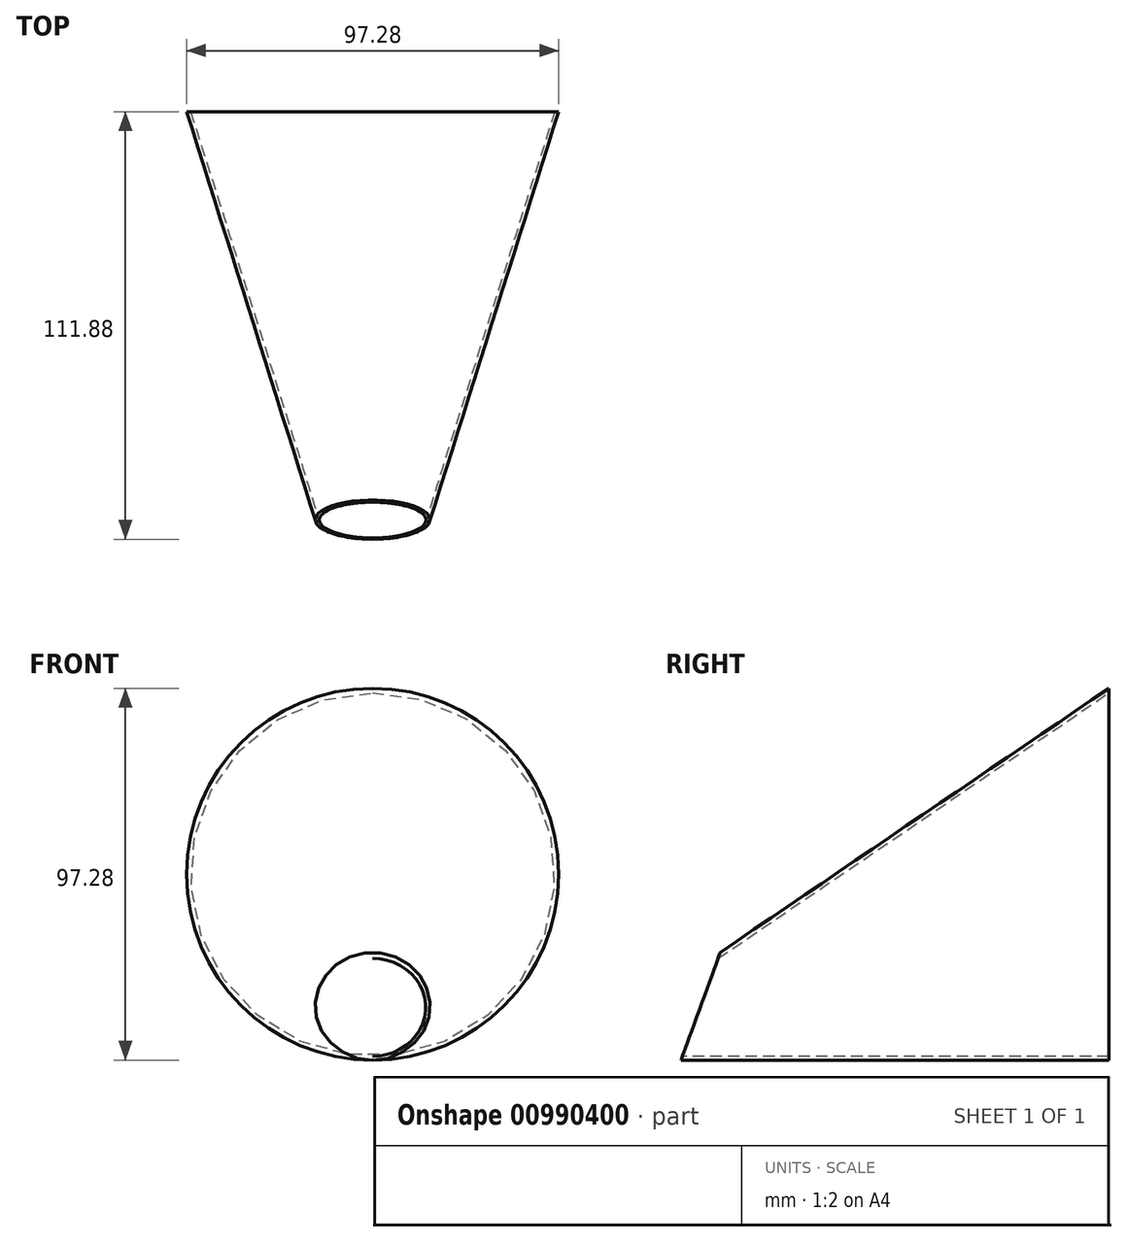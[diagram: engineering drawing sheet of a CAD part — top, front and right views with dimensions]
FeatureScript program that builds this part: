
annotation { "Feature Type Name" : "Feature", "Feature Type Description" : "" }
export const myFeature = defineFeature(function(context is Context, id is Id, definition is map)
    precondition{}
    {
        {
            var Q0;
            Q0=qCreatedBy(makeId("Front.planeOp"),FACE);
            var sketch = newSketch(context, id + "F0", { "sketchPlane" : qUnion([Q0])});
            skCircle(sketch, "E0", {"center": v(0, 0) * mm, "radius": 48.64 * mm});
            skSolve(sketch);
        }
        {
            var Q0;
            Q0=qCreatedBy(makeId("Front.planeOp"),FACE);
            cPlane(context, id + "F1", {"entities" : qUnion([Q0]), "cplaneType" : CPlaneType.OFFSET, "offset" : 112.27 * mm, "width" : 150 * mm, "height" : 150 * mm});
        }
        {
            var Q0;
            Q0=qCreatedBy(id+"F1.planeOp",FACE);
            var sketch = newSketch(context, id + "F2", { "sketchPlane" : qUnion([Q0])});
            skLineSegment(sketch, "E1", {"start": v(-75.93, 0) * mm, "end": v(31.5, 0) * mm});
            skCircle(sketch, "E2.0", {"center": v(0, 0) * mm, "radius": 48.64 * mm, "construction": true});
            skSolve(sketch);
        }
        {
            var Q0;
            Q0=sQuery(id+"F2.wireOp",EDGE,"E1");
            cPlane(context, id + "F3", {"entities" : qUnion([Q0]), "cplaneType" : CPlaneType.LINE_ANGLE, "offset" : 25 * mm, "angle" : 20 * degree, "oppositeDirection" : true, "width" : 150 * mm, "height" : 150 * mm});
        }
        {
            var Q0;
            Q0=qCreatedBy(id+"F3.planeOp",FACE);
            cPlane(context, id + "F4", {"entities" : qUnion([Q0]), "cplaneType" : CPlaneType.OFFSET, "offset" : 17 * mm, "width" : 150 * mm, "height" : 150 * mm});
        }
        {
            var Q0;
            Q0=qCreatedBy(makeId("Right.planeOp"),FACE);
            var sketch = newSketch(context, id + "F5", { "sketchPlane" : qUnion([Q0])});
            skLineSegment(sketch, "E3.0", {"start": v(0, -48.64) * mm, "end": v(0, 48.64) * mm, "construction": true});
            skLineSegment(sketch, "E4", {"start": v(0, -48.64) * mm, "end": v(-237.22, -48.64) * mm, "construction": true});
            skSolve(sketch);
        }
        {
            var Q0;
            Q0=qCreatedBy(id+"F4.planeOp",FACE);
            var sketch = newSketch(context, id + "F6", { "sketchPlane" : qUnion([Q0])});
            skCircle(sketch, "E5", {"center": v(0, -68.97) * mm, "radius": 15 * mm});
            skSolve(sketch);
        }
        {
            var Q0;
            Q0=qCreatedBy(makeId("Right.planeOp"),FACE);
            var sketch = newSketch(context, id + "F7", { "sketchPlane" : qUnion([Q0])});
            skLineSegment(sketch, "E6", {"start": v(-111.88, -48.64) * mm, "end": v(0, -48.64) * mm});
            skLineSegment(sketch, "E7.0", {"start": v(-101.62, -20.45) * mm, "end": v(-111.88, -48.64) * mm, "construction": true});
            skLineSegment(sketch, "E8.0", {"start": v(0, -48.64) * mm, "end": v(0, 48.64) * mm, "construction": true});
            skLineSegment(sketch, "E9", {"start": v(-101.62, -20.45) * mm, "end": v(0, 48.64) * mm, "construction": true});
            skSolve(sketch);
        }
        {
            var Q0;
            Q0 = qSketchRegion(id + "F6", true);
            var Q1;
            Q1 = qSketchRegion(id + "F0", true);
            var Q2;
            Q2=sQuery(id+"F7.wireOp",EDGE,"E6");
            loft(context, id + "F8", {"addGuides" : true, "sheetProfilesArray" : [{ "sheetProfileEntities" : qUnion([Q0]) }, { "sheetProfileEntities" : qUnion([Q1]) }], "guidesArray" : [{ "guideEntities" : qUnion([Q2]), "guideDerivativeType" : LoftGuideDerivativeType.DEFAULT, "guideDerivativeMagnitude" : 1 }]});
        }
        {
            var Q0;
            Q0=makeQuery(id+"F8.opLoft","CAP_FACE",FACE,{"disambiguationData":[OSD([makeQuery(id+"F6.imprint","IMPRINT",FACE,{"disambiguationData":[TD([[makeQuery(id+"F6.imprint","IMPRINT",EDGE,{"derivedFrom":sQuery(id+"F6.wireOp",EDGE,"E5")}),1.0]])]})])],"isStart":true});
            var Q1;
            Q1=makeQuery(id+"F8.opLoft","CAP_FACE",FACE,{"disambiguationData":[OSD([makeQuery(id+"F0.imprint","IMPRINT",FACE,{"disambiguationData":[TD([[makeQuery(id+"F0.imprint","IMPRINT",EDGE,{"derivedFrom":sQuery(id+"F0.wireOp",EDGE,"E0")}),1.0]])]})])],"isStart":true});
            shell(context, id + "F9", {"entities" : qUnion([Q0, Q1]), "thickness" : 1 * mm});
        }
    });
